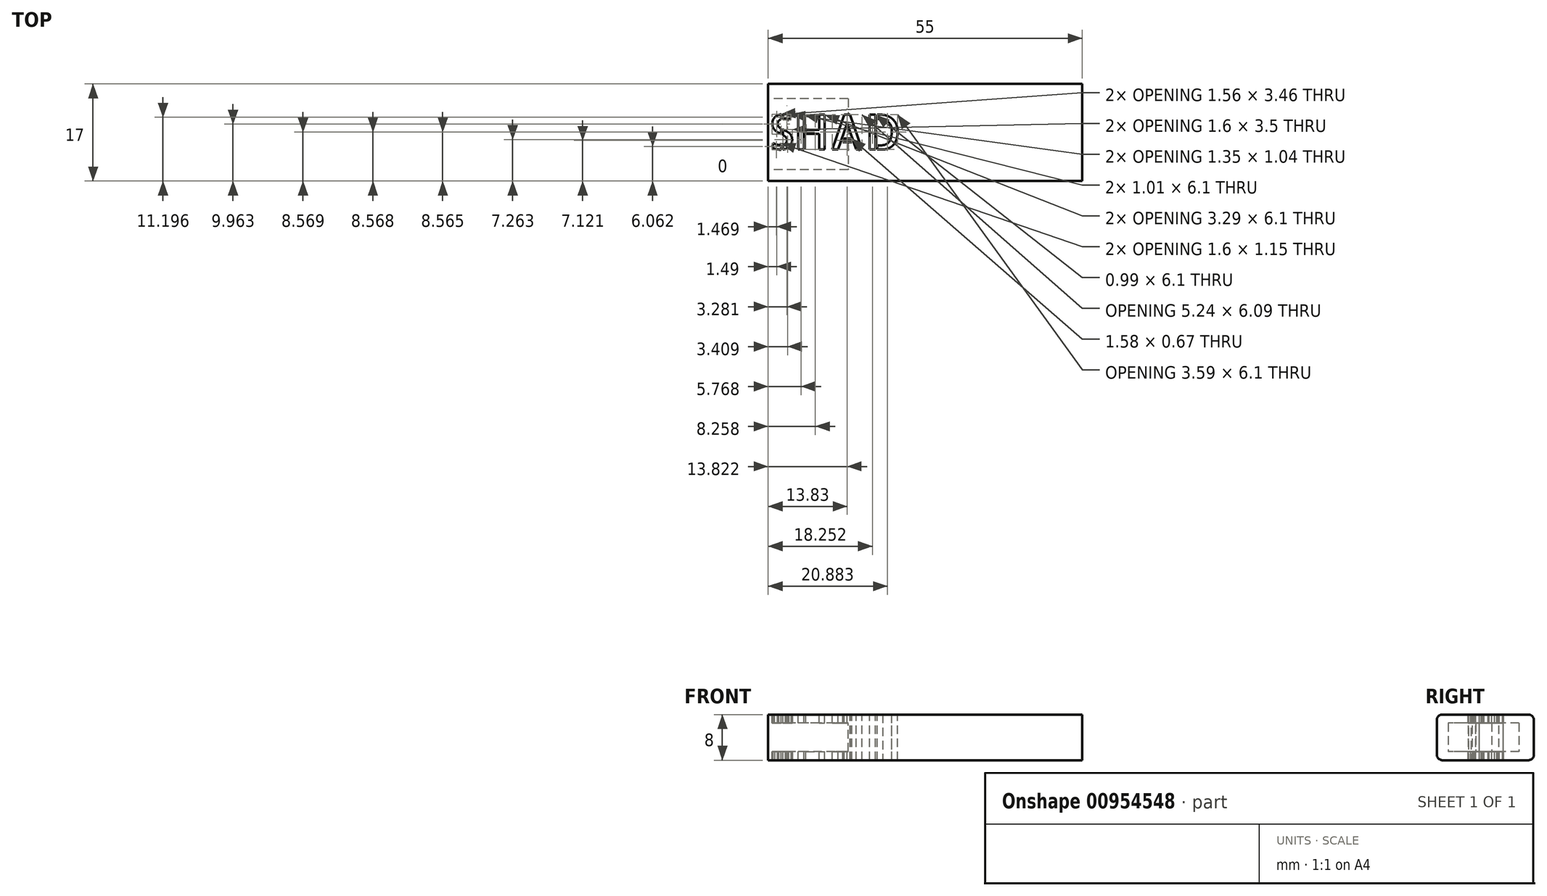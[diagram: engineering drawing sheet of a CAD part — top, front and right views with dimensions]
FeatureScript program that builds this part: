
annotation { "Feature Type Name" : "Feature", "Feature Type Description" : "" }
export const myFeature = defineFeature(function(context is Context, id is Id, definition is map)
    precondition{}
    {
        {
            var Q0;
            Q0=qCreatedBy(makeId("Front.planeOp"),FACE);
            var sketch = newSketch(context, id + "F0", { "sketchPlane" : qUnion([Q0])});
            skLineSegment(sketch, "E0.bottom", {"start": v(7.5, 4) * mm, "end": v(-7.5, 4) * mm});
            skLineSegment(sketch, "E0.top", {"start": v(7.5, -4) * mm, "end": v(-7.5, -4) * mm});
            skLineSegment(sketch, "E0.left", {"start": v(8.5, 3) * mm, "end": v(8.5, -3) * mm});
            skLineSegment(sketch, "E0.right", {"start": v(-8.5, 3) * mm, "end": v(-8.5, -3) * mm});
            skPoint(sketch, "E0.middle", {"position": v(0, 0) * mm});
            skPoint(sketch, "E1.visualSharp", {"position": v(-8.5, 4) * mm});
            skArc(sketch, "E1.filletArc", {"start": v(-7.5, 4) * mm, "mid": v(-8.2, 3.7) * mm, "end": v(-8.5, 3) * mm});
            skPoint(sketch, "E2.visualSharp", {"position": v(8.5, 4) * mm});
            skArc(sketch, "E2.filletArc", {"start": v(8.5, 3) * mm, "mid": v(8.2, 3.7) * mm, "end": v(7.5, 4) * mm});
            skPoint(sketch, "E3.visualSharp", {"position": v(-8.5, -4) * mm});
            skArc(sketch, "E3.filletArc", {"start": v(-8.5, -3) * mm, "mid": v(-8.2, -3.7) * mm, "end": v(-7.5, -4) * mm});
            skPoint(sketch, "E4.visualSharp", {"position": v(8.5, -4) * mm});
            skArc(sketch, "E4.filletArc", {"start": v(7.5, -4) * mm, "mid": v(8.2, -3.7) * mm, "end": v(8.5, -3) * mm});
            skSolve(sketch);
        }
        {
            var Q0;
            Q0 = qSketchRegion(id + "F0", true);
            extrude(context, id + "F1", {"entities" : qUnion([Q0]), "depth" : 55 * mm, "offsetDistance" : 25 * mm});
        }
        {
            var Q0;
            Q0=makeQuery(id+"F1.opExtrude","CAP_FACE",FACE,{"disambiguationData":[OSD([sQuery(id+"F0.wireOp",EDGE,"E0.bottom"),sQuery(id+"F0.wireOp",EDGE,"E0.top"),sQuery(id+"F0.wireOp",EDGE,"E0.left"),sQuery(id+"F0.wireOp",EDGE,"E0.right"),sQuery(id+"F0.wireOp",EDGE,"E1.filletArc"),sQuery(id+"F0.wireOp",EDGE,"E2.filletArc"),sQuery(id+"F0.wireOp",EDGE,"E3.filletArc"),sQuery(id+"F0.wireOp",EDGE,"E4.filletArc")])],"isStart":false});
            var sketch = newSketch(context, id + "F2", { "sketchPlane" : qUnion([Q0])});
            skLineSegment(sketch, "E5.bottom", {"start": v(-5.9, 2.5) * mm, "end": v(6.5, 2.5) * mm});
            skLineSegment(sketch, "E5.top", {"start": v(-5.9, -2.5) * mm, "end": v(6.5, -2.5) * mm});
            skLineSegment(sketch, "E5.left", {"start": v(-5.9, 2.5) * mm, "end": v(-5.9, -2.5) * mm});
            skLineSegment(sketch, "E5.right", {"start": v(6.5, 2.5) * mm, "end": v(6.5, -2.5) * mm});
            skPoint(sketch, "E5.middle", {"position": v(0.3, 0) * mm});
            skSolve(sketch);
        }
        {
            var Q0;
            Q0 = qSketchRegion(id + "F2", true);
            extrude(context, id + "F3", {"entities" : qUnion([Q0]), "operationType" : NewBodyOperationType.REMOVE, "oppositeDirection" : true, "depth" : 14 * mm, "offsetDistance" : 25 * mm});
        }
        {
            var Q0;
            Q0=makeQuery(id+"F1.opExtrude","SWEPT_BODY",BODY,{"disambiguationData":[OSD([sQuery(id+"F0.wireOp",EDGE,"E0.bottom"),sQuery(id+"F0.wireOp",EDGE,"E0.top"),sQuery(id+"F0.wireOp",EDGE,"E0.left"),sQuery(id+"F0.wireOp",EDGE,"E0.right"),sQuery(id+"F0.wireOp",EDGE,"E1.filletArc"),sQuery(id+"F0.wireOp",EDGE,"E2.filletArc"),sQuery(id+"F0.wireOp",EDGE,"E3.filletArc"),sQuery(id+"F0.wireOp",EDGE,"E4.filletArc")])]});
            var Q1;
            Q1=makeQuery(id+"F1.opExtrude","CAP_EDGE",EDGE,{"disambiguationData":[OSD([sQuery(id+"F0.wireOp",EDGE,"E0.left")])],"isStart":true});
            transform(context, id + "F4", {"entities" : qUnion([Q0]), "transformType" : TransformType.ROTATION, "transformAxis" : qUnion([Q1]), "angle" : 90 * degree, "makeCopy" : false});
        }
        {
            var Q0;
            Q0=makeQuery(id+"F1.opExtrude","SWEPT_FACE",FACE,{"disambiguationData":[OSD([sQuery(id+"F0.wireOp",EDGE,"E0.bottom")])]});
            var sketch = newSketch(context, id + "F5", { "sketchPlane" : qUnion([Q0])});
            skText(sketch, "E6", { "text": "SHAD", "fontName": "AllertaStencil-Regular.ttf"});
            const initialGuessF5  = {"E6": [-0.0465, 0.00552, 1, 0, 0.0061]};
            skSetInitialGuess(sketch, initialGuessF5);
            skSolve(sketch);
        }
        {
            var Q0;
            Q0 = qSketchRegion(id + "F5", true);
            extrude(context, id + "F6", {"entities" : qUnion([Q0]), "operationType" : NewBodyOperationType.REMOVE, "oppositeDirection" : true, "depth" : 8 * mm, "offsetDistance" : 25 * mm});
        }
    });
